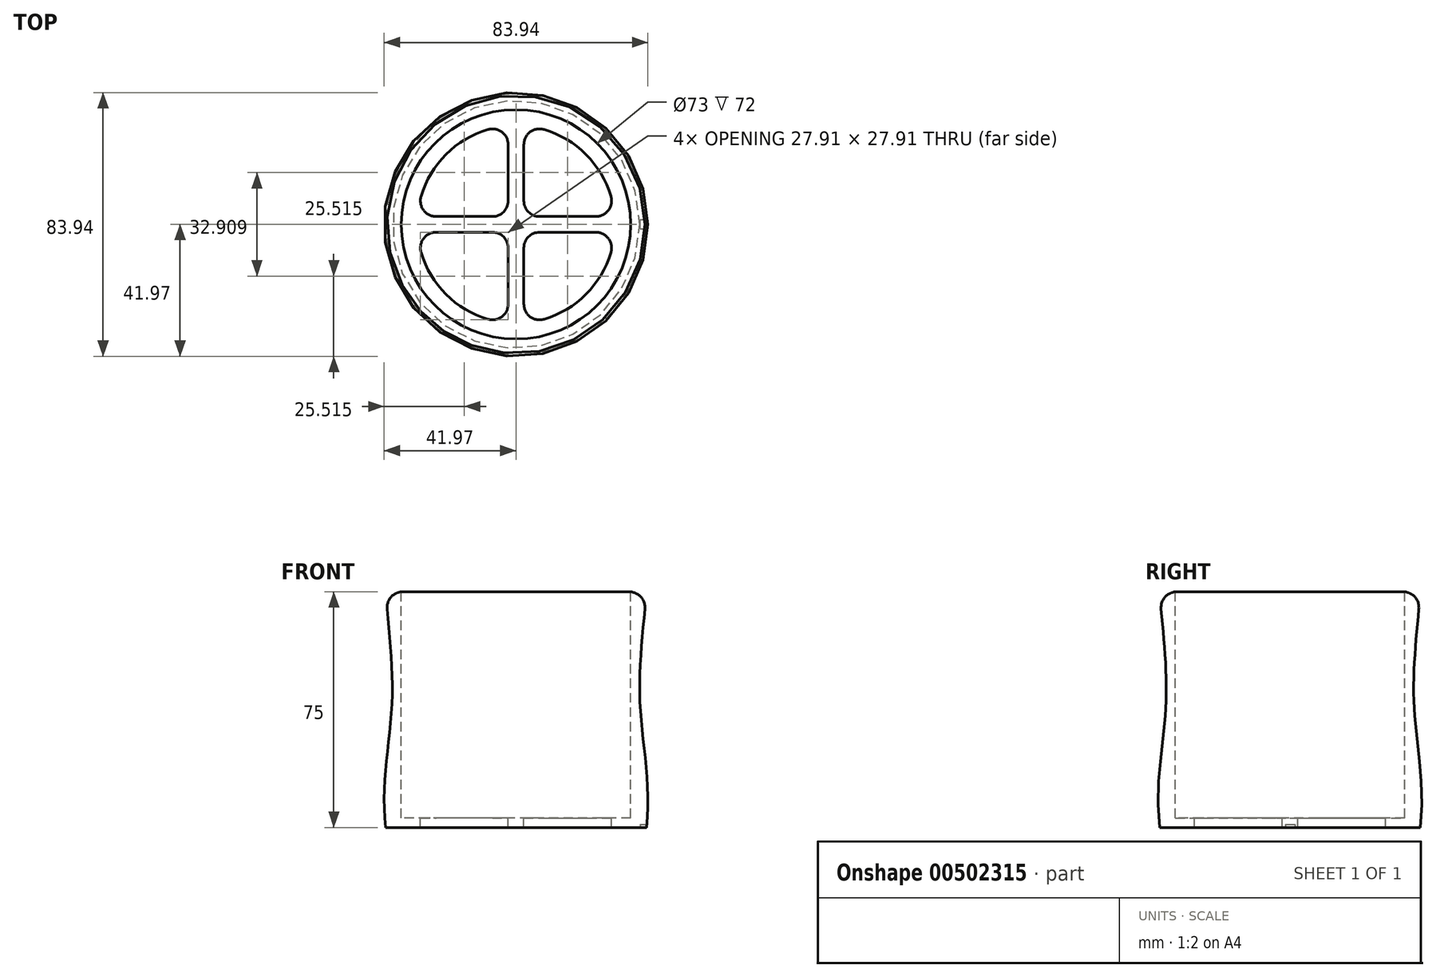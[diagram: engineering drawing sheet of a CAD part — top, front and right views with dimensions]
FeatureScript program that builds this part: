
annotation { "Feature Type Name" : "Feature", "Feature Type Description" : "" }
export const myFeature = defineFeature(function(context is Context, id is Id, definition is map)
    precondition{}
    {
        {
            var Q0;
            Q0=qCreatedBy(makeId("Front.planeOp"),FACE);
            var sketch = newSketch(context, id + "F0", { "sketchPlane" : qUnion([Q0])});
            skLineSegment(sketch, "E0.top", {"start": v(36.5, -36) * mm, "end": v(0, -36) * mm});
            skLineSegment(sketch, "E0.left", {"start": v(36.5, 36) * mm, "end": v(36.5, 0) * mm});
            skPoint(sketch, "E0.middle", {"position": v(0, 0) * mm});
            skPoint(sketch, "E0.right.start.orphan", {"position": v(-36.5, 36) * mm});
            skPoint(sketch, "E1.end.orphan", {"position": v(-36.5, -36) * mm});
            skPoint(sketch, "E0.bottom.end.orphan", {"position": v(0, 36) * mm});
            skLineSegment(sketch, "E2.0", {"start": v(36.5, -39) * mm, "end": v(0, -39) * mm});
            skLineSegment(sketch, "E3", {"start": v(36.5, 0) * mm, "end": v(36.5, -36) * mm});
            skLineSegment(sketch, "E4", {"start": v(36.5, 0) * mm, "end": v(39.5, 0) * mm, "construction": true});
            skLineSegment(sketch, "E5", {"start": v(36.5, 36) * mm, "end": v(41.5, 36) * mm});
            skLineSegment(sketch, "E6", {"start": v(36.5, -39) * mm, "end": v(41.5, -39) * mm});
            skLineSegment(sketch, "E7", {"start": v(0, -36) * mm, "end": v(0, -39) * mm});
            skFitSpline(sketch, "E8", {"points": [v(41.5, 36) * mm, v(39.5, 0) * mm, v(41.5, -39) * mm], "startDerivative": vector(-6.04, -72.73) * mm, "endDerivative": vector(-9.45, -83.83) * mm});
            skSolve(sketch);
        }
        {
            var Q0;
            Q0=makeQuery(id+"F0.imprint","IMPRINT",FACE,{"disambiguationData":[TD([[makeQuery(id+"F0.imprint","IMPRINT",EDGE,{"derivedFrom":sQuery(id+"F0.wireOp",EDGE,"E0.top")}),1.0]])]});
            var Q1;
            Q1=sQuery(id+"F0.wireOp",EDGE,"E7");
            revolve(context, id + "F1", {"entities" : qUnion([Q0]), "axis" : qUnion([Q1]), "revolveType" : RevolveType.FULL});
        }
        {
            var Q0;
            Q0=makeQuery(id+"F1.opRevolve","SWEPT_EDGE",EDGE,{"disambiguationData":[OSD([sQuery(id+"F0.wireOp",EDGE,"E5"),sQuery(id+"F0.wireOp",EDGE,"E8")])]});
            fillet(context, id + "F2", {"entities" : qUnion([Q0]), "radius" : 5 * mm, "tangentPropagation" : true, "allowEdgeOverflow" : false});
        }
        {
            var Q0;
            Q0=makeQuery(id+"F1.opRevolve","SWEPT_FACE",FACE,{"disambiguationData":[OSD([sQuery(id+"F0.wireOp",EDGE,"E2.0"),sQuery(id+"F0.wireOp",EDGE,"E6")])]});
            var sketch = newSketch(context, id + "F3", { "sketchPlane" : qUnion([Q0])});
            skLineSegment(sketch, "E9", {"start": v(42.5, 0) * mm, "end": v(73.8, 0) * mm, "construction": true});
            skLineSegment(sketch, "E10.right", {"start": v(42.5, 1.45) * mm, "end": v(42.5, -1.55) * mm});
            skLineSegment(sketch, "E11.0", {"start": v(39.5, 1.45) * mm, "end": v(39.5, -1.55) * mm});
            skLineSegment(sketch, "E12", {"start": v(39.5, 1.45) * mm, "end": v(42.5, 1.45) * mm});
            skLineSegment(sketch, "E13", {"start": v(39.5, -1.55) * mm, "end": v(42.5, -1.55) * mm});
            skSolve(sketch);
        }
        {
            var Q0;
            {var subQ0=sQuery(id+"F3.wireOp",EDGE,"E11.0");Q0=makeQuery(id+"F3.imprint","IMPRINT",FACE,{"disambiguationData":[TD([[makeQuery(id+"F3.imprint","IMPRINT",EDGE,{"derivedFrom":subQ0}),1.0]])]});}
            extrude(context, id + "F4", {"entities" : qUnion([Q0]), "operationType" : NewBodyOperationType.REMOVE, "oppositeDirection" : true, "depth" : 1 * mm, "offsetDistance" : 25 * mm});
        }
        {
            var Q0;
            Q0=makeQuery(id+"F1.opRevolve","SWEPT_FACE",FACE,{"disambiguationData":[OSD([sQuery(id+"F0.wireOp",EDGE,"E0.top")])]});
            var sketch = newSketch(context, id + "F5", { "sketchPlane" : qUnion([Q0])});
            skArc(sketch, "E14.0", {"start": v(-8.92, 30.21) * mm, "mid": v(-22.27, 22.27) * mm, "end": v(-30.21, 8.92) * mm});
            skLineSegment(sketch, "E15.0", {"start": v(-25.42, 2.5) * mm, "end": v(-7.5, 2.5) * mm});
            skLineSegment(sketch, "E15.1", {"start": v(-2.5, 25.42) * mm, "end": v(-2.5, 7.5) * mm});
            skArc(sketch, "E16.filletArc", {"start": v(-2.5, 25.42) * mm, "mid": v(-4.5, 29.42) * mm, "end": v(-8.92, 30.21) * mm});
            skArc(sketch, "E17.filletArc", {"start": v(-30.21, 8.92) * mm, "mid": v(-29.42, 4.5) * mm, "end": v(-25.42, 2.5) * mm});
            skPoint(sketch, "E18.visualSharp", {"position": v(-2.5, 2.5) * mm});
            skArc(sketch, "E18.filletArc", {"start": v(-7.5, 2.5) * mm, "mid": v(-3.96, 3.96) * mm, "end": v(-2.5, 7.5) * mm});
            skLineSegment(sketch, "E19.1.0", {"start": v(-2.5, -25.42) * mm, "end": v(-2.5, -7.5) * mm});
            skLineSegment(sketch, "E19.1.1", {"start": v(-25.42, -2.5) * mm, "end": v(-7.5, -2.5) * mm});
            skArc(sketch, "E19.1.2", {"start": v(-25.42, -2.5) * mm, "mid": v(-29.42, -4.5) * mm, "end": v(-30.21, -8.92) * mm});
            skArc(sketch, "E19.1.3", {"start": v(-30.21, -8.92) * mm, "mid": v(-22.27, -22.27) * mm, "end": v(-8.92, -30.21) * mm});
            skArc(sketch, "E19.1.4", {"start": v(-2.5, -7.5) * mm, "mid": v(-3.96, -3.96) * mm, "end": v(-7.5, -2.5) * mm});
            skArc(sketch, "E19.1.5", {"start": v(-8.92, -30.21) * mm, "mid": v(-4.5, -29.42) * mm, "end": v(-2.5, -25.42) * mm});
            skPoint(sketch, "E19.1.6", {"position": v(-2.5, -2.5) * mm});
            skLineSegment(sketch, "E19.2.0", {"start": v(25.42, -2.5) * mm, "end": v(7.5, -2.5) * mm});
            skLineSegment(sketch, "E19.2.1", {"start": v(2.5, -25.42) * mm, "end": v(2.5, -7.5) * mm});
            skArc(sketch, "E19.2.2", {"start": v(2.5, -25.42) * mm, "mid": v(4.5, -29.42) * mm, "end": v(8.92, -30.21) * mm});
            skArc(sketch, "E19.2.3", {"start": v(8.92, -30.21) * mm, "mid": v(22.27, -22.27) * mm, "end": v(30.21, -8.92) * mm});
            skArc(sketch, "E19.2.4", {"start": v(7.5, -2.5) * mm, "mid": v(3.96, -3.96) * mm, "end": v(2.5, -7.5) * mm});
            skArc(sketch, "E19.2.5", {"start": v(30.21, -8.92) * mm, "mid": v(29.42, -4.5) * mm, "end": v(25.42, -2.5) * mm});
            skPoint(sketch, "E19.2.6", {"position": v(2.5, -2.5) * mm});
            skLineSegment(sketch, "E20.1.3.0", {"start": v(2.5, 25.42) * mm, "end": v(2.5, 7.5) * mm});
            skLineSegment(sketch, "E20.3.3.0", {"start": v(25.42, 2.5) * mm, "end": v(7.5, 2.5) * mm});
            skArc(sketch, "E20.6.3.0", {"start": v(25.42, 2.5) * mm, "mid": v(29.42, 4.5) * mm, "end": v(30.21, 8.92) * mm});
            skArc(sketch, "E20.10.3.0", {"start": v(30.21, 8.92) * mm, "mid": v(22.27, 22.27) * mm, "end": v(8.92, 30.21) * mm});
            skArc(sketch, "E20.14.3.0", {"start": v(2.5, 7.5) * mm, "mid": v(3.96, 3.96) * mm, "end": v(7.5, 2.5) * mm});
            skArc(sketch, "E20.18.3.0", {"start": v(8.92, 30.21) * mm, "mid": v(4.5, 29.42) * mm, "end": v(2.5, 25.42) * mm});
            skPoint(sketch, "E20.22.3.0", {"position": v(2.5, 2.5) * mm});
            skSolve(sketch);
        }
        {
            var Q0;
            Q0 = qSketchRegion(id + "F5", true);
            extrude(context, id + "F6", {"entities" : qUnion([Q0]), "operationType" : NewBodyOperationType.REMOVE, "endBound" : BoundingType.SYMMETRIC, "oppositeDirection" : true, "depth" : 150 * mm, "offsetDistance" : 25 * mm});
        }
    });
